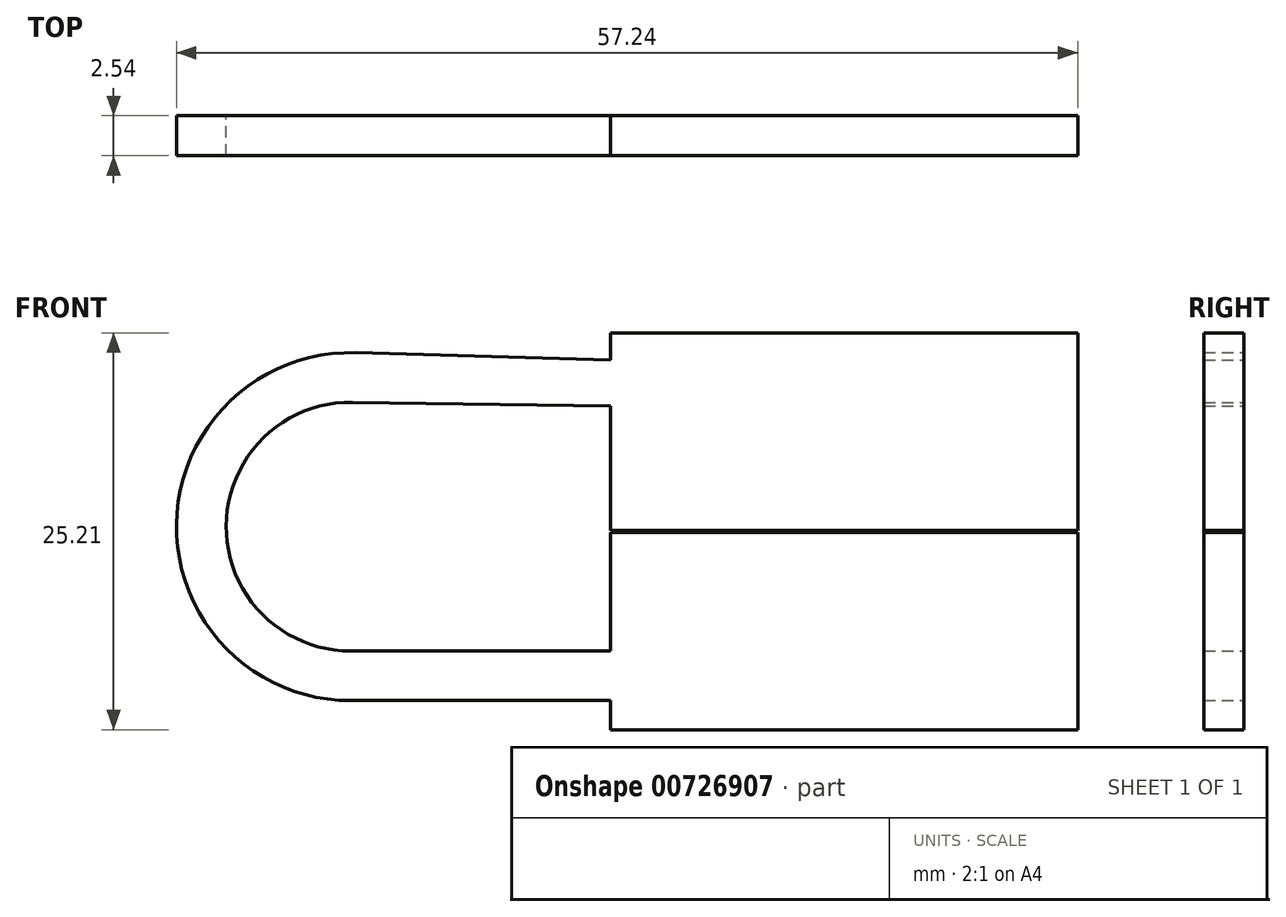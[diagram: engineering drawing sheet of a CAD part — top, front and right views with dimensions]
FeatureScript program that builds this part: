
annotation { "Feature Type Name" : "Feature", "Feature Type Description" : "" }
export const myFeature = defineFeature(function(context is Context, id is Id, definition is map)
    precondition{}
    {
        {
            var Q0;
            Q0=qCreatedBy(makeId("Front.planeOp"),FACE);
            var sketch = newSketch(context, id + "F0", { "sketchPlane" : qUnion([Q0])});
            skLineSegment(sketch, "E0.bottom", {"start": v(-29.46, 37.5) * mm, "end": v(0.22, 37.5) * mm});
            skLineSegment(sketch, "E0.top", {"start": v(-29.46, 24.96) * mm, "end": v(0.22, 24.96) * mm});
            skLineSegment(sketch, "E0.left", {"start": v(-29.46, 37.5) * mm, "end": v(-29.46, 24.96) * mm});
            skLineSegment(sketch, "E0.right", {"start": v(0.22, 37.5) * mm, "end": v(0.22, 24.96) * mm});
            skLineSegment(sketch, "E1.bottom", {"start": v(-29.46, 24.83) * mm, "end": v(0.22, 24.83) * mm});
            skLineSegment(sketch, "E1.top", {"start": v(-29.46, 12.3) * mm, "end": v(0.22, 12.3) * mm});
            skLineSegment(sketch, "E1.left", {"start": v(-29.46, 24.83) * mm, "end": v(-29.46, 12.3) * mm});
            skLineSegment(sketch, "E1.right", {"start": v(0.22, 24.83) * mm, "end": v(0.22, 12.3) * mm});
            skArc(sketch, "E2", {"start": v(-45.85, 33.09) * mm, "mid": v(-53.87, 25.24) * mm, "end": v(-45.95, 17.3) * mm});
            skArc(sketch, "E3", {"start": v(-45.65, 36.24) * mm, "mid": v(-57.02, 25.34) * mm, "end": v(-45.95, 14.14) * mm});
            skLineSegment(sketch, "E4", {"start": v(-45.65, 36.24) * mm, "end": v(-29.46, 35.76) * mm});
            skLineSegment(sketch, "E5", {"start": v(-45.85, 33.09) * mm, "end": v(-29.46, 32.85) * mm});
            skLineSegment(sketch, "E6", {"start": v(-45.95, 17.3) * mm, "end": v(-29.46, 17.3) * mm});
            skLineSegment(sketch, "E7", {"start": v(-45.95, 14.14) * mm, "end": v(-29.46, 14.14) * mm});
            skSolve(sketch);
        }
        {
            var Q0;
            {var subQ3=sQuery(id+"F0.wireOp",EDGE,"E0.bottom");Q0=makeQuery(id+"F0.imprint","IMPRINT",FACE,{"disambiguationData":[TD([[makeQuery(id+"F0.imprint","IMPRINT",EDGE,{"derivedFrom":subQ3}),-1.0]])]});}
            var Q1;
            {var subQ3=sQuery(id+"F0.wireOp",EDGE,"E1.bottom");Q1=makeQuery(id+"F0.imprint","IMPRINT",FACE,{"disambiguationData":[TD([[makeQuery(id+"F0.imprint","IMPRINT",EDGE,{"derivedFrom":subQ3}),-1.0]])]});}
            var Q2;
            Q2=makeQuery(id+"F0.imprint","IMPRINT",FACE,{"disambiguationData":[TD([[makeQuery(id+"F0.imprint","IMPRINT",EDGE,{"derivedFrom":sQuery(id+"F0.wireOp",EDGE,"E2")}),-1.0]])]});
            extrude(context, id + "F1", {"entities" : qUnion([Q0, Q1, Q2]), "depth" : 2.54 * mm, "offsetDistance" : 25.4 * mm});
        }
    });
